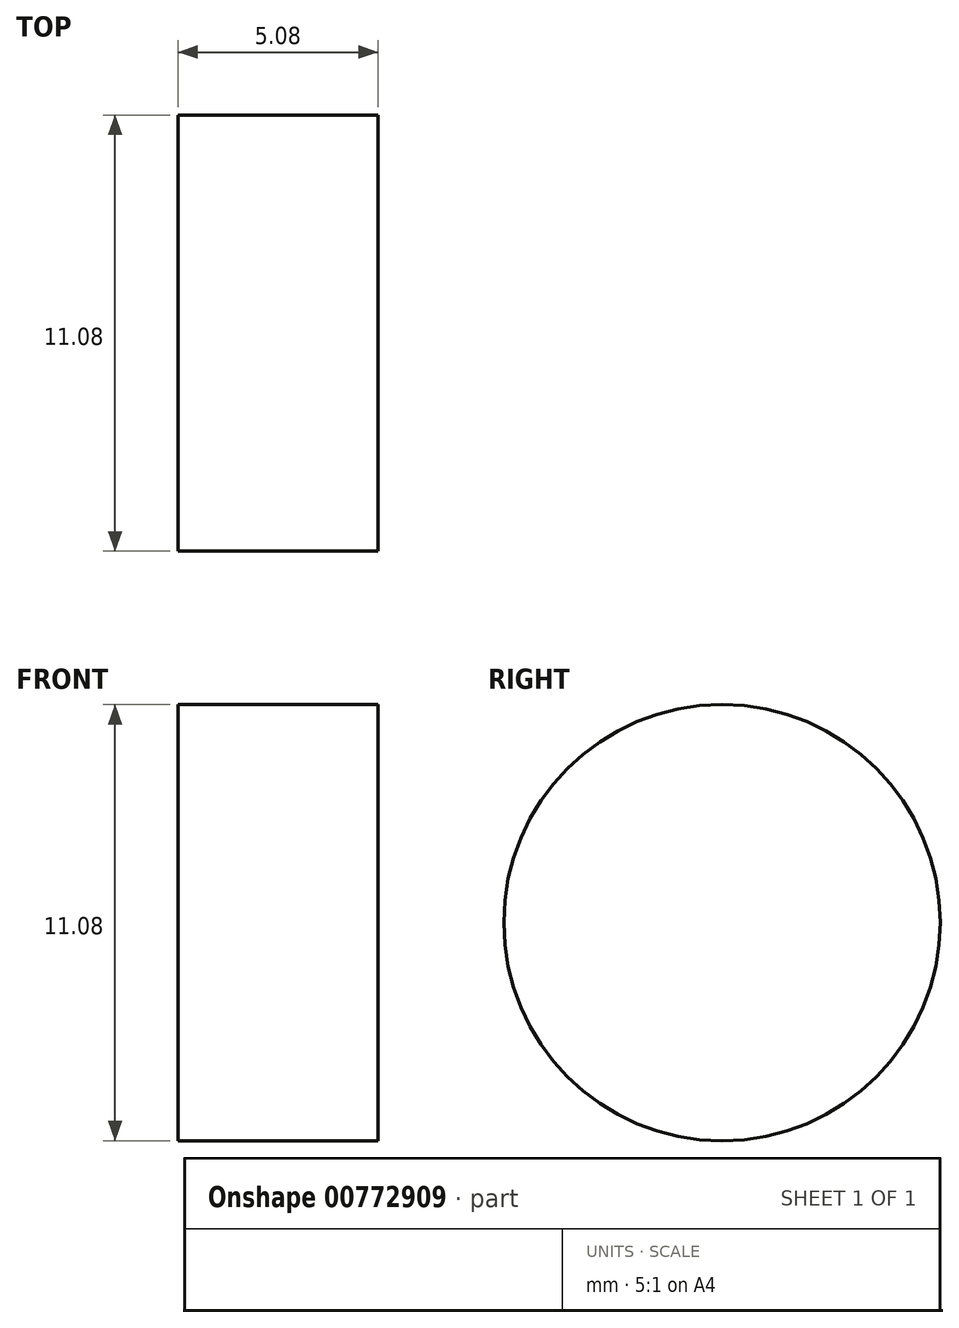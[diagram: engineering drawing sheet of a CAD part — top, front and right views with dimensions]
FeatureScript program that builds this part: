
annotation { "Feature Type Name" : "Feature", "Feature Type Description" : "" }
export const myFeature = defineFeature(function(context is Context, id is Id, definition is map)
    precondition{}
    {
        {
            var Q0;
            Q0=qCreatedBy(makeId("Right.planeOp"),FACE);
            var sketch = newSketch(context, id + "F0", { "sketchPlane" : qUnion([Q0])});
            skCircle(sketch, "E0", {"center": v(-33.02, 17.15) * mm, "radius": 5.54 * mm});
            skSolve(sketch);
        }
        {
            var Q0;
            Q0 = qSketchRegion(id + "F0", true);
            extrude(context, id + "F1", {"entities" : qUnion([Q0]), "depth" : 5.08 * mm, "offsetDistance" : 25.4 * mm});
        }
    });
